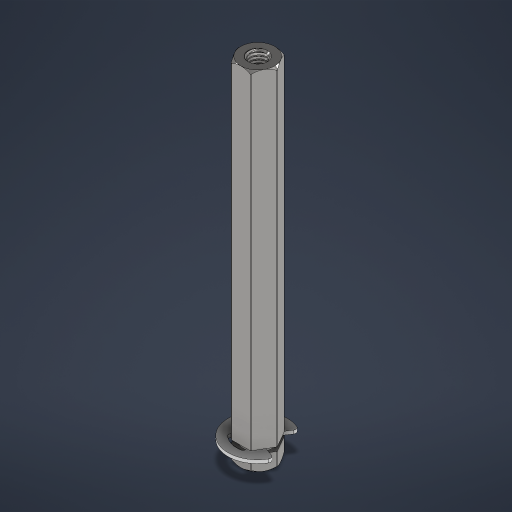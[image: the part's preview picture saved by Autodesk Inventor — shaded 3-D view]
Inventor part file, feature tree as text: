
AUTODESK INVENTOR PART (.ipt)
format: ipt  version: 2024 (Build 280153000, 153)  size: 977,408 bytes
history: native  units: in
note: dims shown in document units (in); Inventor stores cm internally (conversion verified against a paired STEP export)
features: plane x1, other x1
ambient origin geometry x8: Origin, YZ Plane, XZ Plane, XY Plane, X Axis, Y Axis, Z Axis, Center Point
bodies: Solid1 (feature_tree), Solid2 (feature_tree)
feature tree (2):
  plane  "Work Plane1"
  other  "2106 Series 8mm REX e-clip_2:1"
